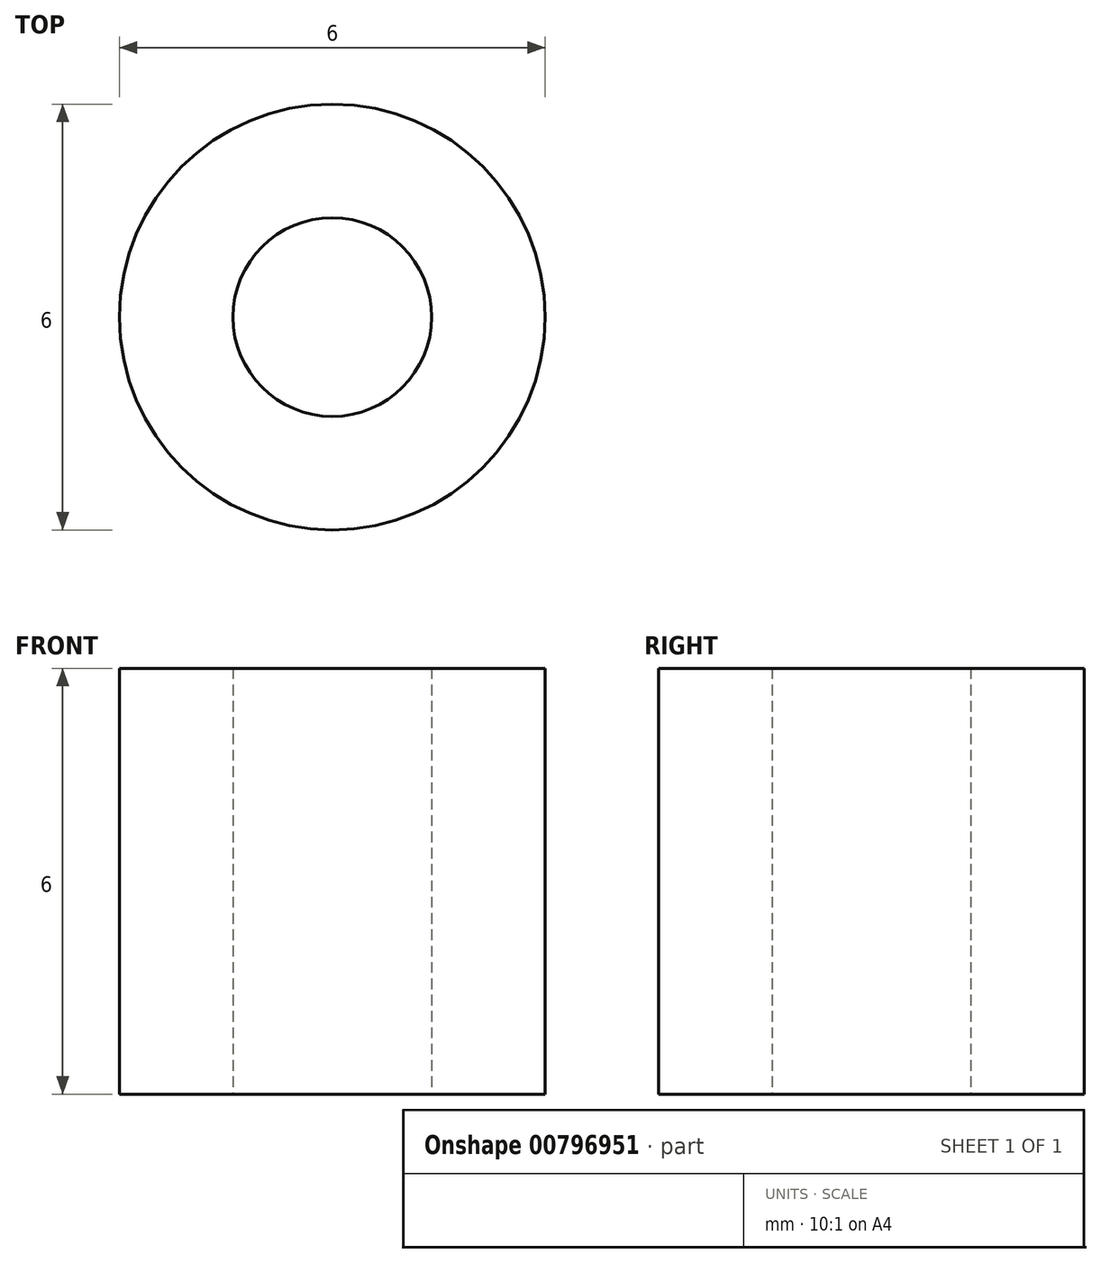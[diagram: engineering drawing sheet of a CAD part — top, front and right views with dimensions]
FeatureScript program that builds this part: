
annotation { "Feature Type Name" : "Feature", "Feature Type Description" : "" }
export const myFeature = defineFeature(function(context is Context, id is Id, definition is map)
    precondition{}
    {
        {
            var Q0;
            Q0=qCreatedBy(makeId("Top.planeOp"),FACE);
            var sketch = newSketch(context, id + "F0", { "sketchPlane" : qUnion([Q0])});
            skCircle(sketch, "E0", {"center": v(0, 0) * mm, "radius": 3 * mm});
            skCircle(sketch, "E1", {"center": v(0, 0) * mm, "radius": 1.4 * mm});
            skSolve(sketch);
        }
        {
            var Q0;
            Q0 = qSketchRegion(id + "F0", true);
            extrude(context, id + "F1", {"entities" : qUnion([Q0]), "depth" : 6 * mm, "offsetDistance" : 25 * mm});
        }
    });
